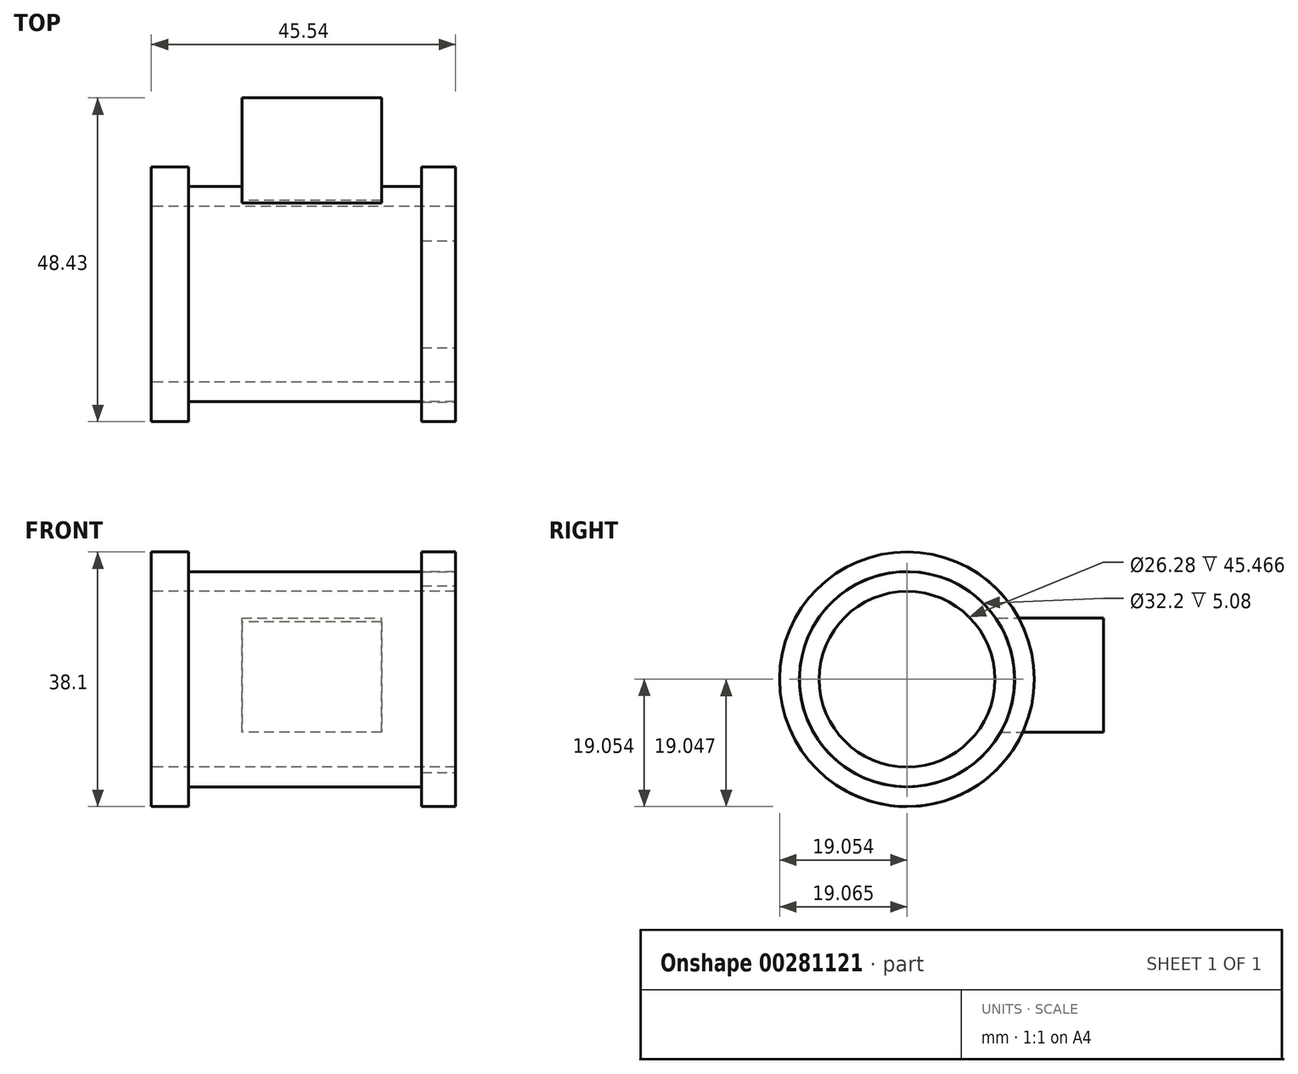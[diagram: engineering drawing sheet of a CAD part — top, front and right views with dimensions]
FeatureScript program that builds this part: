
annotation { "Feature Type Name" : "Feature", "Feature Type Description" : "" }
export const myFeature = defineFeature(function(context is Context, id is Id, definition is map)
    precondition{}
    {
        {
            var Q0;
            Q0=qCreatedBy(makeId("Right.planeOp"),FACE);
            var sketch = newSketch(context, id + "F0", { "sketchPlane" : qUnion([Q0])});
            skCircle(sketch, "E0", {"center": v(-29.36, 37.43) * mm, "radius": 19.05 * mm});
            skCircle(sketch, "E1", {"center": v(-29.36, 37.43) * mm, "radius": 16.1 * mm});
            skCircle(sketch, "E2", {"center": v(-29.36, 37.43) * mm, "radius": 13.14 * mm});
            skSolve(sketch);
        }
        {
            var Q0;
            Q0=makeQuery(id+"F0.imprint","IMPRINT",FACE,{"disambiguationData":[TD([[makeQuery(id+"F0.imprint","IMPRINT",EDGE,{"derivedFrom":sQuery(id+"F0.wireOp",EDGE,"E0")}),1.0]])]});
            extrude(context, id + "F1", {"entities" : qUnion([Q0]), "depth" : 5.6 * mm});
        }
        {
            var Q0;
            Q0=makeQuery(id+"F0.imprint","IMPRINT",FACE,{"disambiguationData":[TD([[makeQuery(id+"F0.imprint","IMPRINT",EDGE,{"derivedFrom":sQuery(id+"F0.wireOp",EDGE,"E1")}),1.0]])]});
            extrude(context, id + "F2", {"entities" : qUnion([Q0]), "operationType" : NewBodyOperationType.ADD, "depth" : 45.47 * mm});
        }
        {
            var Q0;
            Q0=qCreatedBy(makeId("Right.planeOp"),FACE);
            cPlane(context, id + "F3", {"entities" : qUnion([Q0]), "cplaneType" : CPlaneType.OFFSET, "offset" : 45.54 * mm, "width" : 152.4 * mm, "height" : 152.4 * mm});
        }
        {
            var Q0;
            Q0=qCreatedBy(id+"F3.planeOp",FACE);
            var sketch = newSketch(context, id + "F4", { "sketchPlane" : qUnion([Q0])});
            skCircle(sketch, "E3", {"center": v(-29.38, 37.43) * mm, "radius": 19.05 * mm});
            skCircle(sketch, "E4", {"center": v(-29.38, 37.43) * mm, "radius": 16.1 * mm});
            skSolve(sketch);
        }
        {
            var Q0;
            Q0=makeQuery(id+"F4.imprint","IMPRINT",FACE,{"disambiguationData":[TD([[makeQuery(id+"F4.imprint","IMPRINT",EDGE,{"derivedFrom":sQuery(id+"F4.wireOp",EDGE,"E3")}),1.0]])]});
            extrude(context, id + "F5", {"entities" : qUnion([Q0]), "operationType" : NewBodyOperationType.ADD, "oppositeDirection" : true, "depth" : 5.08 * mm});
        }
        {
            var Q0;
            Q0=qCreatedBy(makeId("Front.planeOp"),FACE);
            var sketch = newSketch(context, id + "F6", { "sketchPlane" : qUnion([Q0])});
            skLineSegment(sketch, "E5.bottom", {"start": v(13.55, 29.5) * mm, "end": v(34.47, 29.5) * mm});
            skLineSegment(sketch, "E5.top", {"start": v(13.55, 46.6) * mm, "end": v(34.47, 46.6) * mm});
            skLineSegment(sketch, "E5.left", {"start": v(13.55, 29.5) * mm, "end": v(13.55, 46.6) * mm});
            skLineSegment(sketch, "E5.right", {"start": v(34.47, 29.5) * mm, "end": v(34.47, 46.6) * mm});
            skPoint(sketch, "E5.middle", {"position": v(24, 38.05) * mm});
            skSolve(sketch);
        }
        {
            var Q0;
            Q0=makeQuery(id+"F6.imprint","IMPRINT",FACE,{"disambiguationData":[TD([[makeQuery(id+"F6.imprint","IMPRINT",EDGE,{"derivedFrom":sQuery(id+"F6.wireOp",EDGE,"E5.bottom")}),1.0]])]});
            extrude(context, id + "F7", {"entities" : qUnion([Q0]), "operationType" : NewBodyOperationType.ADD, "depth" : 15.75 * mm});
        }
    });
